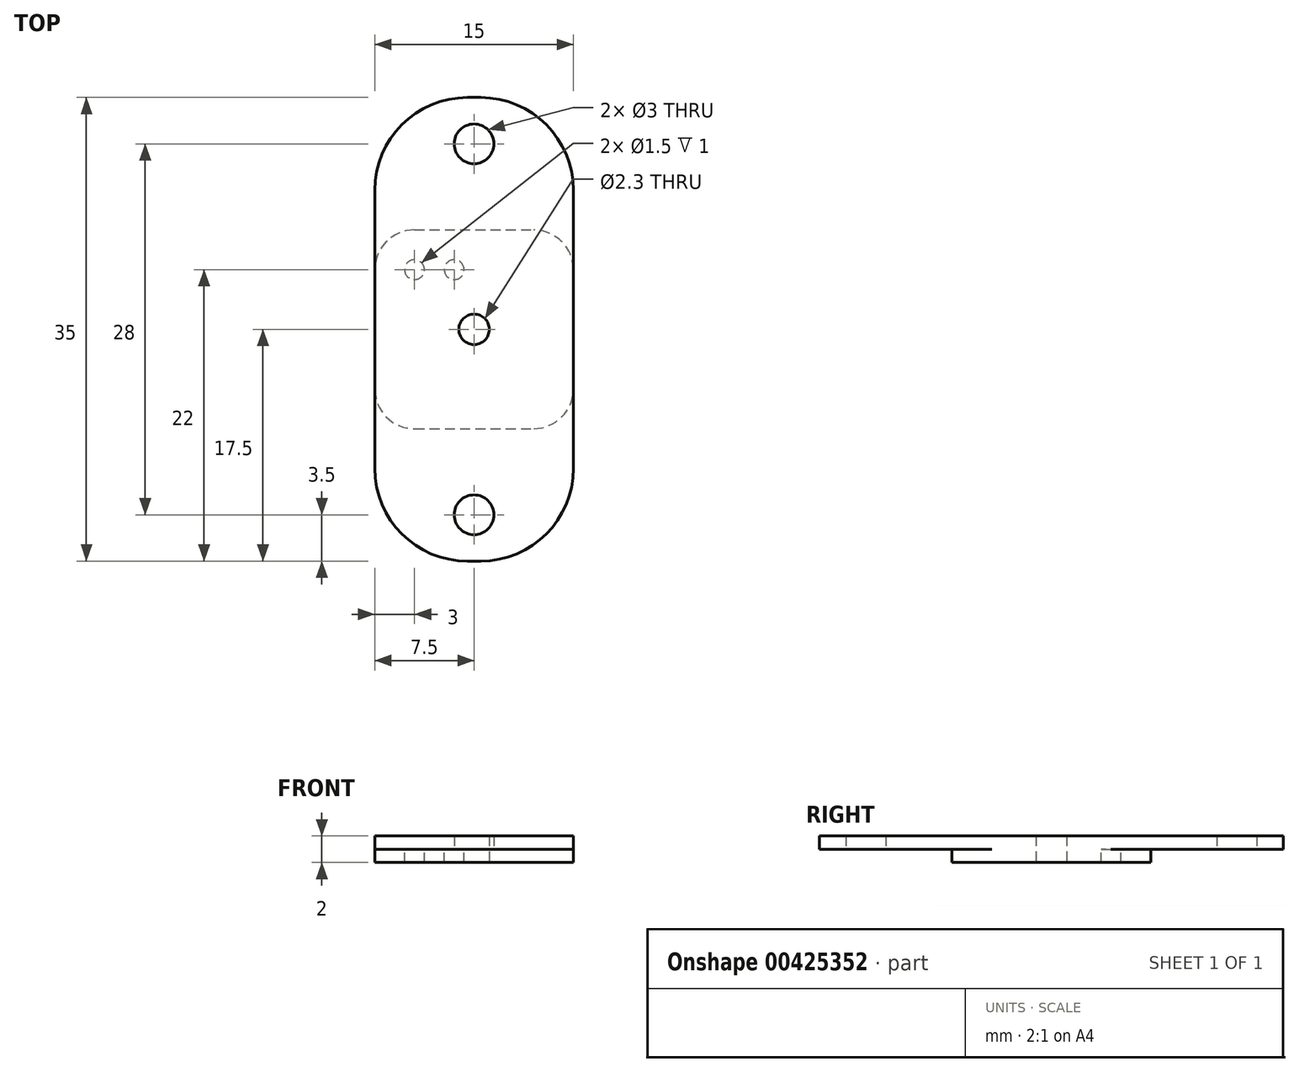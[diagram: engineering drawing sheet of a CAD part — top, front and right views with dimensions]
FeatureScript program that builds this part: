
annotation { "Feature Type Name" : "Feature", "Feature Type Description" : "" }
export const myFeature = defineFeature(function(context is Context, id is Id, definition is map)
    precondition{}
    {
        {
            var Q0;
            Q0=qCreatedBy(makeId("Top.planeOp"),FACE);
            var sketch = newSketch(context, id + "F0", { "sketchPlane" : qUnion([Q0])});
            skCircle(sketch, "E0", {"center": v(0, 0) * mm, "radius": 1.15 * mm});
            skCircle(sketch, "E1", {"center": v(0, 0) * mm, "radius": 2.5 * mm});
            skSolve(sketch);
        }
        {
            var Q0;
            Q0=makeQuery(id+"F0.imprint","IMPRINT",FACE,{"disambiguationData":[TD([[makeQuery(id+"F0.imprint","IMPRINT",EDGE,{"derivedFrom":sQuery(id+"F0.wireOp",EDGE,"E0")}),-1.0]])]});
            extrude(context, id + "F1", {"entities" : qUnion([Q0]), "depth" : 1 * mm});
        }
        {
            var Q0;
            Q0=makeQuery(id+"F1.opExtrude","CAP_FACE",FACE,{"disambiguationData":[OSD([sQuery(id+"F0.wireOp",EDGE,"E0"),sQuery(id+"F0.wireOp",EDGE,"E1")])],"isStart":true});
            var sketch = newSketch(context, id + "F2", { "sketchPlane" : qUnion([Q0])});
            skCircle(sketch, "E2", {"center": v(0, 0) * mm, "radius": 1.15 * mm});
            skCircle(sketch, "E3", {"center": v(0, 0) * mm, "radius": 5 * mm});
            skLineSegment(sketch, "E4.bottom", {"start": v(-7.5, -7.5) * mm, "end": v(7.5, -7.5) * mm});
            skLineSegment(sketch, "E4.top", {"start": v(-7.5, 7.5) * mm, "end": v(7.5, 7.5) * mm});
            skLineSegment(sketch, "E4.left", {"start": v(-7.5, -7.5) * mm, "end": v(-7.5, 7.5) * mm});
            skLineSegment(sketch, "E4.right", {"start": v(7.5, -7.5) * mm, "end": v(7.5, 7.5) * mm});
            skSolve(sketch);
        }
        {
            var Q0;
            Q0=makeQuery(id+"F2.imprint","IMPRINT",FACE,{"disambiguationData":[TD([[makeQuery(id+"F2.imprint","IMPRINT",EDGE,{"derivedFrom":sQuery(id+"F2.wireOp",EDGE,"E3")}),-1.0]])]});
            var Q1;
            Q1=makeQuery(id+"F2.imprint","IMPRINT",FACE,{"disambiguationData":[TD([[makeQuery(id+"F2.imprint","IMPRINT",EDGE,{"derivedFrom":sQuery(id+"F2.wireOp",EDGE,"E3")}),1.0]])]});
            var Q2;
            Q2=makeQuery(id+"F2.imprint","IMPRINT",FACE,{"disambiguationData":[TD([[makeQuery(id+"F2.imprint","IMPRINT",EDGE,{"derivedFrom":sQuery(id+"F2.wireOp",EDGE,"E2")}),1.0]])]});
            extrude(context, id + "F3", {"entities" : qUnion([Q0, Q1, Q2]), "operationType" : NewBodyOperationType.ADD, "depth" : 1 * mm});
        }
        {
            var Q0;
            Q0=makeQuery(id+"F3.opExtrude","SWEPT_EDGE",EDGE,{"disambiguationData":[OSD([sQuery(id+"F2.wireOp",EDGE,"E4.bottom"),sQuery(id+"F2.wireOp",EDGE,"E4.left")])]});
            var Q1;
            Q1=makeQuery(id+"F3.opExtrude","SWEPT_EDGE",EDGE,{"disambiguationData":[OSD([sQuery(id+"F2.wireOp",EDGE,"E4.bottom"),sQuery(id+"F2.wireOp",EDGE,"E4.right")])]});
            var Q2;
            Q2=makeQuery(id+"F3.opExtrude","SWEPT_EDGE",EDGE,{"disambiguationData":[OSD([sQuery(id+"F2.wireOp",EDGE,"E4.top"),sQuery(id+"F2.wireOp",EDGE,"E4.left")])]});
            var Q3;
            Q3=makeQuery(id+"F3.opExtrude","SWEPT_EDGE",EDGE,{"disambiguationData":[OSD([sQuery(id+"F2.wireOp",EDGE,"E4.top"),sQuery(id+"F2.wireOp",EDGE,"E4.right")])]});
            fillet(context, id + "F4", {"entities" : qUnion([Q0, Q1, Q2, Q3]), "radius" : 3 * mm, "tangentPropagation" : true, "allowEdgeOverflow" : false});
        }
        {
            var Q0;
            Q0=makeQuery(id+"F3.opExtrude","CAP_FACE",FACE,{"disambiguationData":[OSD([sQuery(id+"F2.wireOp",EDGE,"E2"),sQuery(id+"F2.wireOp",EDGE,"E4.bottom"),sQuery(id+"F2.wireOp",EDGE,"E4.top"),sQuery(id+"F2.wireOp",EDGE,"E4.left"),sQuery(id+"F2.wireOp",EDGE,"E4.right")])],"isStart":true});
            var sketch = newSketch(context, id + "F5", { "sketchPlane" : qUnion([Q0])});
            skCircle(sketch, "E5", {"center": v(-4.5, 4.5) * mm, "radius": 0.75 * mm});
            skCircle(sketch, "E6", {"center": v(-1.5, 4.5) * mm, "radius": 0.75 * mm});
            skSolve(sketch);
        }
        {
            var Q0;
            Q0=makeQuery(id+"F5.imprint","IMPRINT",FACE,{"disambiguationData":[TD([[makeQuery(id+"F5.imprint","IMPRINT",EDGE,{"derivedFrom":sQuery(id+"F5.wireOp",EDGE,"E5")}),-1.0]])]});
            var sketch = newSketch(context, id + "F6", { "sketchPlane" : qUnion([Q0])});
            skLineSegment(sketch, "E7.bottom", {"start": v(7.5, -17.5) * mm, "end": v(-7.5, -17.5) * mm});
            skLineSegment(sketch, "E7.top", {"start": v(7.5, 17.5) * mm, "end": v(-7.5, 17.5) * mm});
            skLineSegment(sketch, "E7.left", {"start": v(7.5, -17.5) * mm, "end": v(7.5, 17.5) * mm});
            skLineSegment(sketch, "E7.right", {"start": v(-7.5, -17.5) * mm, "end": v(-7.5, 17.5) * mm});
            skPoint(sketch, "E7.middle", {"position": v(0, 0) * mm});
            skCircle(sketch, "E8", {"center": v(0, 14) * mm, "radius": 1.5 * mm});
            skCircle(sketch, "E9", {"center": v(0, -14) * mm, "radius": 1.5 * mm});
            skCircle(sketch, "E10", {"center": v(0, 0) * mm, "radius": 1.15 * mm});
            skSolve(sketch);
        }
        {
            var Q0;
            Q0 = qSketchRegion(id + "F6", true);
            extrude(context, id + "F7", {"entities" : qUnion([Q0]), "operationType" : NewBodyOperationType.ADD, "depth" : 1 * mm});
        }
        {
            var Q0;
            Q0=makeQuery(id+"F7.opExtrude","SWEPT_EDGE",EDGE,{"disambiguationData":[OSD([sQuery(id+"F6.wireOp",EDGE,"E7.top"),sQuery(id+"F6.wireOp",EDGE,"E7.right")])]});
            var Q1;
            Q1=makeQuery(id+"F7.opExtrude","SWEPT_EDGE",EDGE,{"disambiguationData":[OSD([sQuery(id+"F6.wireOp",EDGE,"E7.top"),sQuery(id+"F6.wireOp",EDGE,"E7.left")])]});
            var Q2;
            Q2=makeQuery(id+"F7.opExtrude","SWEPT_EDGE",EDGE,{"disambiguationData":[OSD([sQuery(id+"F6.wireOp",EDGE,"E7.bottom"),sQuery(id+"F6.wireOp",EDGE,"E7.left")])]});
            var Q3;
            Q3=makeQuery(id+"F7.opExtrude","SWEPT_EDGE",EDGE,{"disambiguationData":[OSD([sQuery(id+"F6.wireOp",EDGE,"E7.bottom"),sQuery(id+"F6.wireOp",EDGE,"E7.right")])]});
            fillet(context, id + "F8", {"entities" : qUnion([Q0, Q1, Q2, Q3]), "radius" : 7 * mm, "tangentPropagation" : true, "allowEdgeOverflow" : false});
        }
        {
            var Q0;
            Q0=qSketchRegion(id+"F5",true);
            extrude(context, id + "F9", {"entities" : qUnion([Q0]), "operationType" : NewBodyOperationType.REMOVE, "oppositeDirection" : true, "depth" : 25 * mm});
        }
    });
